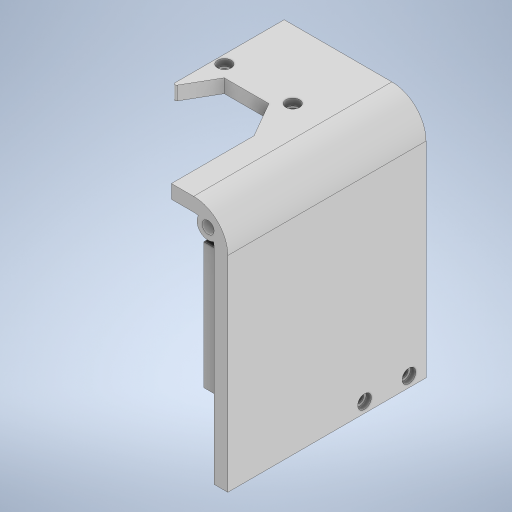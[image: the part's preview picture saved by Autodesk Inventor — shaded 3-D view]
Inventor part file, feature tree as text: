
AUTODESK INVENTOR PART (.ipt)
format: ipt  version: 2023 (Build 270158000, 158)  size: 361,984 bytes
history: native  units: mm
features: extrude x12, sketch x10, projected_geometry x2, other x1, fillet x1
ambient origin geometry x8: Origin, YZ Plane, XZ Plane, XY Plane, X Axis, Y Axis, Z Axis, Center Point
bodies: Body1 (feature_tree)
feature tree (26):
  other  "솔리드1"
  extrude  "돌출1"  Depth=70.0mm
  extrude  "돌출2"  Depth=41.5mm
  extrude  "돌출3"  Depth=4.0mm
  extrude  "돌출4"  TaperAngle=90.0deg  [1 undecoded]
  extrude  "돌출5"  Depth=6.0mm
  fillet  "모깎기2"  Radius=10.0mm
  sketch  "스케치6"
  extrude  "돌출6"  Depth=23.0mm TaperAngle=0.0deg
  extrude  "돌출7"  Depth=6.0mm
  sketch  "스케치7"
  extrude  "돌출8"  Depth=2.5mm
  extrude  "돌출9"  Depth=2.5mm
  extrude  "돌출10"  Depth=5.0mm
  extrude  "돌출11"  Depth=5.0mm
  extrude  "돌출12"  TaperAngle=0.0deg  [1 undecoded]
  sketch  "스케치1"
  sketch  "스케치2"
  sketch  "스케치3"
  sketch  "스케치4"
  sketch  "스케치5"
  projected_geometry  "투영된 루프1"
  sketch  "스케치8"
  sketch  "스케치9"
  projected_geometry  "투영된 루프2"
  sketch  "스케치10"
note: 2 required parameter values undecoded (feature->parameter linkage not recoverable at this tier; creation-order binding heuristic only, values carry confidence <= 0.55)
